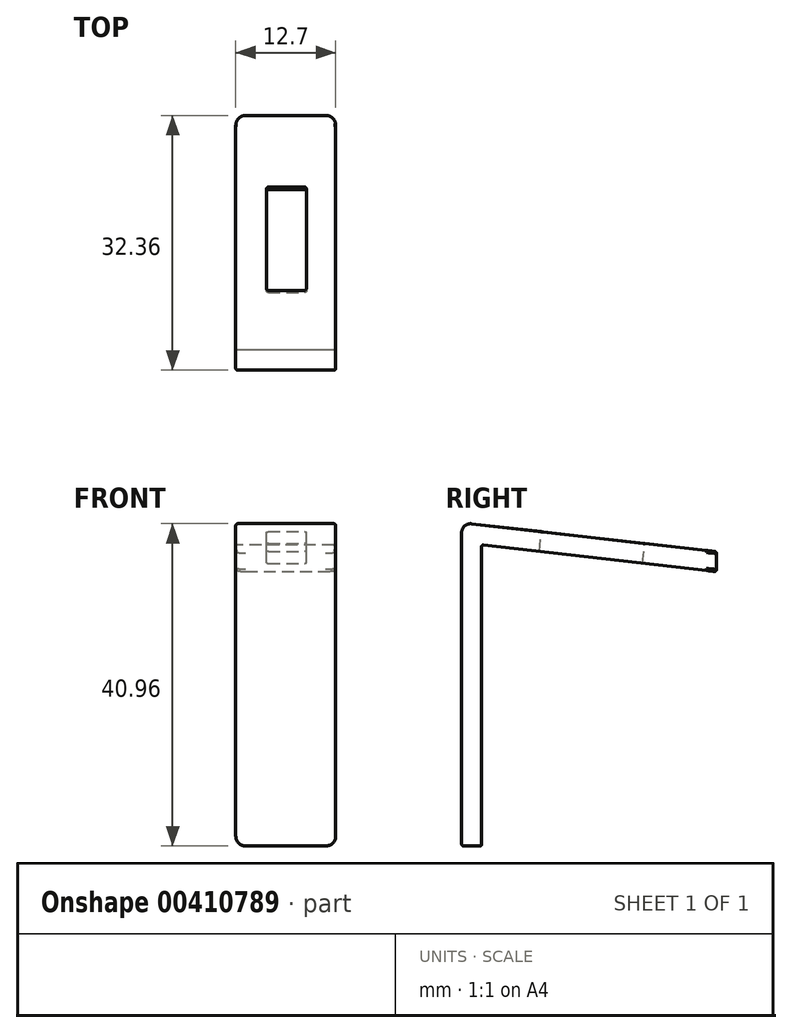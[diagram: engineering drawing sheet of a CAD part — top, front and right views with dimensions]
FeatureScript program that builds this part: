
annotation { "Feature Type Name" : "Feature", "Feature Type Description" : "" }
export const myFeature = defineFeature(function(context is Context, id is Id, definition is map)
    precondition{}
    {
        {
            var Q0;
            Q0=qCreatedBy(makeId("Right.planeOp"),FACE);
            var sketch = newSketch(context, id + "F0", { "sketchPlane" : qUnion([Q0])});
            skLineSegment(sketch, "E0", {"start": v(9.25, 16.44) * mm, "end": v(-20.35, 19.82) * mm});
            skLineSegment(sketch, "E1", {"start": v(-20.57, 19.62) * mm, "end": v(-20.57, -18.42) * mm});
            skLineSegment(sketch, "E2", {"start": v(9.25, 16.44) * mm, "end": v(9.25, 18.98) * mm});
            skLineSegment(sketch, "E3", {"start": v(9.25, 18.98) * mm, "end": v(-21.85, 22.53) * mm});
            skLineSegment(sketch, "E4", {"start": v(-23.11, 21.4) * mm, "end": v(-23.11, -18.42) * mm});
            skLineSegment(sketch, "E5", {"start": v(-23.11, -18.42) * mm, "end": v(-20.57, -18.42) * mm});
            skPoint(sketch, "E6.visualSharp", {"position": v(-23.11, 22.67) * mm});
            skArc(sketch, "E6.filletArc", {"start": v(-21.85, 22.53) * mm, "mid": v(-22.73, 22.25) * mm, "end": v(-23.11, 21.4) * mm});
            skPoint(sketch, "E7.visualSharp", {"position": v(-20.57, 19.84) * mm});
            skArc(sketch, "E7.filletArc", {"start": v(-20.35, 19.82) * mm, "mid": v(-20.5, 19.77) * mm, "end": v(-20.57, 19.62) * mm});
            skSolve(sketch);
        }
        {
            var Q0;
            Q0=makeQuery(id+"F0.imprint","IMPRINT",FACE,{"disambiguationData":[TD([[makeQuery(id+"F0.imprint","IMPRINT",EDGE,{"derivedFrom":sQuery(id+"F0.wireOp",EDGE,"E0")}),-1.0]])]});
            extrude(context, id + "F1", {"entities" : qUnion([Q0]), "depth" : 12.7 * mm, "offsetDistance" : 25.4 * mm, "symmetric" : true});
        }
        {
            var Q0;
            Q0=makeQuery(id+"F1.opExtrude","CAP_EDGE",EDGE,{"disambiguationData":[OSD([sQuery(id+"F0.wireOp",EDGE,"E2")])],"isStart":false});
            var Q1;
            Q1=makeQuery(id+"F1.opExtrude","CAP_EDGE",EDGE,{"disambiguationData":[OSD([sQuery(id+"F0.wireOp",EDGE,"E2")])],"isStart":true});
            var Q2;
            Q2=makeQuery(id+"F1.opExtrude","CAP_EDGE",EDGE,{"disambiguationData":[OSD([sQuery(id+"F0.wireOp",EDGE,"E5")])],"isStart":true});
            var Q3;
            Q3=makeQuery(id+"F1.opExtrude","CAP_EDGE",EDGE,{"disambiguationData":[OSD([sQuery(id+"F0.wireOp",EDGE,"E5")])],"isStart":false});
            fillet(context, id + "F2", {"entities" : qUnion([Q0, Q1, Q2, Q3]), "radius" : 1.27 * mm, "tangentPropagation" : true, "allowEdgeOverflow" : false});
        }
        {
            var Q0;
            Q0=makeQuery(id+"F1.opExtrude","CAP_EDGE",EDGE,{"disambiguationData":[OSD([sQuery(id+"F0.wireOp",EDGE,"E4")])],"isStart":false});
            var Q1;
            Q1=makeQuery(id+"F1.opExtrude","CAP_EDGE",EDGE,{"disambiguationData":[OSD([sQuery(id+"F0.wireOp",EDGE,"E1")])],"isStart":false});
            fillet(context, id + "F3", {"entities" : qUnion([Q0, Q1]), "radius" : 0.25 * mm, "tangentPropagation" : true, "allowEdgeOverflow" : false});
        }
        {
            var Q0;
            Q0=makeQuery(id+"F1.opExtrude","SWEPT_FACE",FACE,{"disambiguationData":[OSD([sQuery(id+"F0.wireOp",EDGE,"E3")])]});
            var sketch = newSketch(context, id + "F4", { "sketchPlane" : qUnion([Q0])});
            skLineSegment(sketch, "E8.bottom", {"start": v(-2.2, -2.12) * mm, "end": v(2.37, -2.12) * mm});
            skLineSegment(sketch, "E8.top", {"start": v(-2.2, -15.33) * mm, "end": v(2.37, -15.33) * mm});
            skLineSegment(sketch, "E8.left", {"start": v(-2.46, -2.38) * mm, "end": v(-2.46, -15.08) * mm});
            skLineSegment(sketch, "E8.right", {"start": v(2.62, -2.38) * mm, "end": v(2.62, -15.08) * mm});
            skPoint(sketch, "E9.visualSharp", {"position": v(-2.46, -2.12) * mm});
            skArc(sketch, "E9.filletArc", {"start": v(-2.2, -2.12) * mm, "mid": v(-2.38, -2.2) * mm, "end": v(-2.46, -2.38) * mm});
            skPoint(sketch, "E10.visualSharp", {"position": v(2.62, -2.12) * mm});
            skArc(sketch, "E10.filletArc", {"start": v(2.62, -2.38) * mm, "mid": v(2.55, -2.2) * mm, "end": v(2.37, -2.12) * mm});
            skPoint(sketch, "E11.visualSharp", {"position": v(2.62, -15.33) * mm});
            skArc(sketch, "E11.filletArc", {"start": v(2.37, -15.33) * mm, "mid": v(2.55, -15.26) * mm, "end": v(2.62, -15.08) * mm});
            skPoint(sketch, "E12.visualSharp", {"position": v(-2.46, -15.33) * mm});
            skArc(sketch, "E12.filletArc", {"start": v(-2.46, -15.08) * mm, "mid": v(-2.38, -15.26) * mm, "end": v(-2.2, -15.33) * mm});
            skSolve(sketch);
        }
        {
            var Q0;
            {var subQ4=sQuery(id+"F4.wireOp",EDGE,"E8.left");Q0=makeQuery(id+"F4.imprint","IMPRINT",FACE,{"disambiguationData":[TD([[makeQuery(id+"F4.imprint","IMPRINT",EDGE,{"derivedFrom":subQ4}),1.0]])]});}
            extrude(context, id + "F5", {"entities" : qUnion([Q0]), "operationType" : NewBodyOperationType.REMOVE, "endBound" : BoundingType.UP_TO_NEXT, "oppositeDirection" : true, "depth" : 25.4 * mm, "offsetDistance" : 25.4 * mm});
        }
    });
